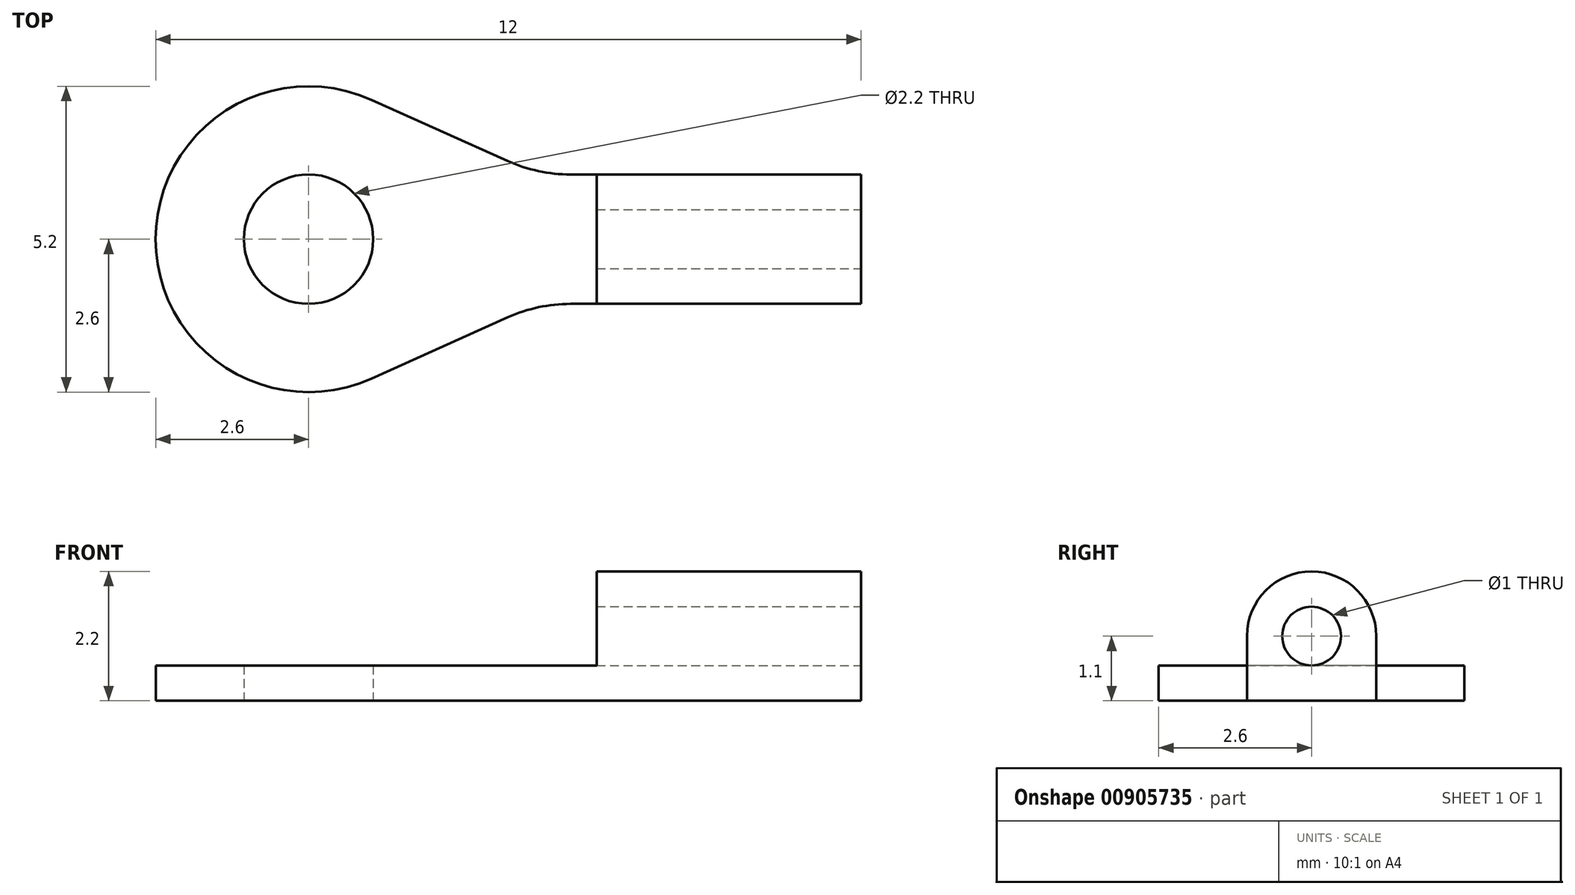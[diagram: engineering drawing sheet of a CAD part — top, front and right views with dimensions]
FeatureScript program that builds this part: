
annotation { "Feature Type Name" : "Feature", "Feature Type Description" : "" }
export const myFeature = defineFeature(function(context is Context, id is Id, definition is map)
    precondition{}
    {
        {
            var Q0;
            Q0=qCreatedBy(makeId("Top.planeOp"),FACE);
            var sketch = newSketch(context, id + "F0", { "sketchPlane" : qUnion([Q0])});
            skLineSegment(sketch, "E0", {"start": v(12, 1.5) * mm, "end": v(12, 3.7) * mm});
            skLineSegment(sketch, "E1", {"start": v(0, 2.6) * mm, "end": v(0, 2.6) * mm});
            skPoint(sketch, "E2.visualSharp", {"position": v(0, 5.2) * mm});
            skArc(sketch, "E2.filletArc", {"start": v(2.6, 5.2) * mm, "mid": v(0.76, 4.44) * mm, "end": v(0, 2.6) * mm});
            skPoint(sketch, "E3.visualSharp", {"position": v(0, 0) * mm});
            skArc(sketch, "E3.filletArc", {"start": v(0, 2.6) * mm, "mid": v(0.76, 0.76) * mm, "end": v(2.6, 0) * mm});
            skLineSegment(sketch, "E4.0", {"start": v(7.5, 1.5) * mm, "end": v(7.5, 3.7) * mm});
            skLineSegment(sketch, "E5.0", {"start": v(12, 3.7) * mm, "end": v(7.06, 3.7) * mm});
            skLineSegment(sketch, "E6.0", {"start": v(12, 1.5) * mm, "end": v(7.06, 1.5) * mm});
            skCircle(sketch, "E7", {"center": v(2.6, 2.6) * mm, "radius": 1.1 * mm});
            skArc(sketch, "E8", {"start": v(3.66, 4.97) * mm, "mid": v(0, 2.6) * mm, "end": v(3.66, 0.23) * mm});
            skLineSegment(sketch, "E9.0", {"start": v(6.5, 1.44) * mm, "end": v(6.5, 1.5) * mm});
            skLineSegment(sketch, "E10", {"start": v(6, 3.93) * mm, "end": v(3.66, 4.97) * mm});
            skLineSegment(sketch, "E11", {"start": v(6, 1.27) * mm, "end": v(3.66, 0.23) * mm});
            skPoint(sketch, "E12.visualSharp", {"position": v(6.5, 3.7) * mm});
            skArc(sketch, "E12.filletArc", {"start": v(6, 3.93) * mm, "mid": v(6.51, 3.76) * mm, "end": v(7.06, 3.7) * mm});
            skPoint(sketch, "E13.visualSharp", {"position": v(6.5, 1.5) * mm});
            skArc(sketch, "E13.filletArc", {"start": v(7.06, 1.5) * mm, "mid": v(6.51, 1.44) * mm, "end": v(6, 1.27) * mm});
            skPoint(sketch, "E14.orphan", {"position": v(12, 5.2) * mm});
            skPoint(sketch, "E15.orphan", {"position": v(7.5, 5.2) * mm});
            skPoint(sketch, "E16.orphan", {"position": v(7.5, 0) * mm});
            skPoint(sketch, "E17.orphan", {"position": v(12, 0) * mm});
            skPoint(sketch, "E18.end.orphan", {"position": v(7.5, 2.6) * mm});
            skPoint(sketch, "E18.start.orphan", {"position": v(12, 2.6) * mm});
            skLineSegment(sketch, "E19.trimOffspring", {"start": v(6.5, 3.7) * mm, "end": v(6.5, 3.76) * mm});
            skSolve(sketch);
        }
        {
            var Q0;
            {var subQ0=sQuery(id+"F0.wireOp",EDGE,"E0");Q0=makeQuery(id+"F0.imprint","IMPRINT",FACE,{"disambiguationData":[TD([[makeQuery(id+"F0.imprint","IMPRINT",EDGE,{"derivedFrom":subQ0}),1.0]])]});}
            var Q1;
            Q1 = qSketchRegion(id + "F0", true);
            extrude(context, id + "F1", {"entities" : qUnion([Q0, Q1]), "depth" : 0.6 * mm, "offsetDistance" : 25 * mm});
        }
        {
            var Q0;
            Q0=makeQuery(id+"F1.opExtrude","CAP_FACE",FACE,{"disambiguationData":[OSD([sQuery(id+"F0.wireOp",EDGE,"E0"),sQuery(id+"F0.wireOp",EDGE,"E5.0"),sQuery(id+"F0.wireOp",EDGE,"E6.0"),sQuery(id+"F0.wireOp",EDGE,"E7"),sQuery(id+"F0.wireOp",EDGE,"E8"),sQuery(id+"F0.wireOp",EDGE,"E10"),sQuery(id+"F0.wireOp",EDGE,"E11"),sQuery(id+"F0.wireOp",EDGE,"E12.filletArc"),sQuery(id+"F0.wireOp",EDGE,"E13.filletArc")])],"isStart":false});
            var sketch = newSketch(context, id + "F2", { "sketchPlane" : qUnion([Q0])});
            skLineSegment(sketch, "E20.bottom", {"start": v(12, 3.7) * mm, "end": v(7.5, 3.7) * mm});
            skLineSegment(sketch, "E20.top", {"start": v(12, 1.5) * mm, "end": v(7.5, 1.5) * mm});
            skLineSegment(sketch, "E20.left", {"start": v(12, 3.7) * mm, "end": v(12, 1.5) * mm});
            skLineSegment(sketch, "E20.right", {"start": v(7.5, 3.7) * mm, "end": v(7.5, 1.5) * mm});
            skSolve(sketch);
        }
        {
            var Q0;
            Q0 = qSketchRegion(id + "F2", true);
            extrude(context, id + "F3", {"entities" : qUnion([Q0]), "operationType" : NewBodyOperationType.ADD, "depth" : 1.6 * mm, "offsetDistance" : 25 * mm});
        }
        {
            var Q0;
            Q0=makeQuery(id+"F3.opExtrude","CAP_EDGE",EDGE,{"disambiguationData":[OSD([sQuery(id+"F2.wireOp",EDGE,"E20.top")])],"isStart":false});
            var Q1;
            Q1=makeQuery(id+"F3.opExtrude","CAP_EDGE",EDGE,{"disambiguationData":[OSD([sQuery(id+"F2.wireOp",EDGE,"E20.bottom")])],"isStart":false});
            fillet(context, id + "F4", {"entities" : qUnion([Q0, Q1]), "radius" : 1.1 * mm, "tangentPropagation" : true, "allowEdgeOverflow" : false});
        }
        {
            var Q0;
            Q0=makeQuery(id+"F3.boolean.opBoolean","MERGE",FACE,{"derivedFrom":[makeQuery(id+"F1.opExtrude","SWEPT_FACE",FACE,{"disambiguationData":[OSD([sQuery(id+"F0.wireOp",EDGE,"E0")])]}),makeQuery(id+"F3.opExtrude","SWEPT_FACE",FACE,{"disambiguationData":[OSD([sQuery(id+"F2.wireOp",EDGE,"E20.left")])]})]});
            var sketch = newSketch(context, id + "F5", { "sketchPlane" : qUnion([Q0])});
            skCircle(sketch, "E21", {"center": v(2.6, 1.1) * mm, "radius": 0.5 * mm});
            skSolve(sketch);
        }
        {
            var Q0;
            Q0=makeQuery(id+"F5.imprint","IMPRINT",FACE,{"disambiguationData":[TD([[makeQuery(id+"F5.imprint","IMPRINT",EDGE,{"derivedFrom":sQuery(id+"F5.wireOp",EDGE,"E21")}),1.0]])]});
            extrude(context, id + "F6", {"entities" : qUnion([Q0]), "operationType" : NewBodyOperationType.REMOVE, "oppositeDirection" : true, "depth" : 10 * mm, "offsetDistance" : 25 * mm});
        }
    });
